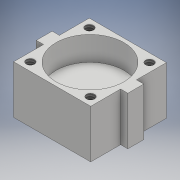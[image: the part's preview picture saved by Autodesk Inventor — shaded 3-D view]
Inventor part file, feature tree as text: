
AUTODESK INVENTOR PART (.ipt)
format: ipt  version: 2018 (Build 220112000, 112)  size: 132,608 bytes
history: native  units: mm
features: sketch x3, extrude x2, hole x1
ambient origin geometry x8: Origin, YZ Plane, XZ Plane, XY Plane, X Axis, Y Axis, Z Axis, Center Point
bodies: Solid1 (feature_tree)
feature tree (6):
  extrude  "Extrusion1"  Depth=15.7mm
  extrude  "Extrusion2"  Depth=3.3mm
  hole  "Hole2"  [1 undecoded]
  sketch  "Sketch1"  dims[d0=16.0mm d1=15.7mm]
  sketch  "Sketch2"  dims[d2=19.0mm d3=3.3mm]
  sketch  "Sketch4"  dims[d4=10.0mm d5=0.0mm d6=14.1mm d7=5.0mm d8=0.0mm d17=17.5mm d18=1.694mm d19=4.369mm d20=4.0mm d21=2.0mm d22=90.0deg d23=6.637mm d24=20.594885mm]
note: 1 required parameter value undecoded (feature->parameter linkage not recoverable at this tier; creation-order binding heuristic only, values carry confidence <= 0.55)
